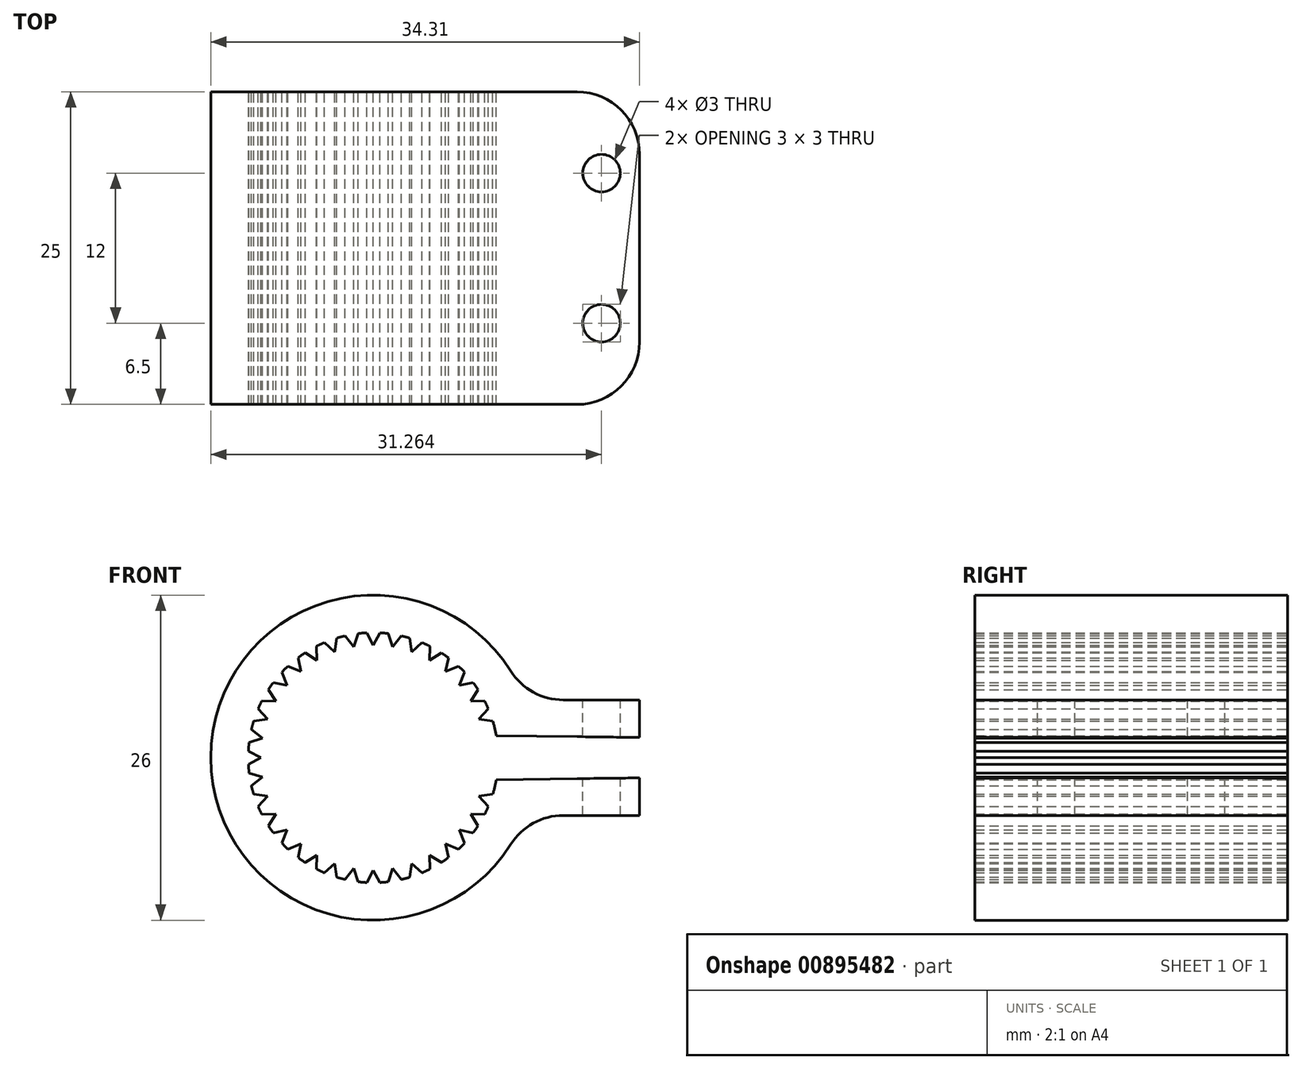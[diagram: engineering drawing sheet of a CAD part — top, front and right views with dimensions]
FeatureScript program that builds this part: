
annotation { "Feature Type Name" : "Feature", "Feature Type Description" : "" }
export const myFeature = defineFeature(function(context is Context, id is Id, definition is map)
    precondition{}
    {
        {
            var Q0;
            Q0=qCreatedBy(makeId("Front.planeOp"),FACE);
            var sketch = newSketch(context, id + "F0", { "sketchPlane" : qUnion([Q0])});
            skArc(sketch, "E0", {"start": v(-3.9, 9.2) * mm, "mid": v(-4.23, 9.06) * mm, "end": v(-4.54, 8.91) * mm});
            skArc(sketch, "E1.0", {"start": v(12.15, 4.62) * mm, "mid": v(-13, 0) * mm, "end": v(12.15, -4.62) * mm});
            skLineSegment(sketch, "E2", {"start": v(-0.52, 9.99) * mm, "end": v(0, 9) * mm});
            skLineSegment(sketch, "E3.MirrorCS", {"start": v(0.52, 9.99) * mm, "end": v(0, 9) * mm});
            skLineSegment(sketch, "E4.1.0", {"start": v(-2.25, 9.74) * mm, "end": v(-1.56, 8.86) * mm});
            skLineSegment(sketch, "E4.1.1", {"start": v(-1.22, 9.93) * mm, "end": v(-1.56, 8.86) * mm});
            skLineSegment(sketch, "E4.2.0", {"start": v(-3.9, 9.2) * mm, "end": v(-3.08, 8.46) * mm});
            skLineSegment(sketch, "E4.2.1", {"start": v(-2.92, 9.56) * mm, "end": v(-3.08, 8.46) * mm});
            skLineSegment(sketch, "E5.2.3.0", {"start": v(-5.45, 8.39) * mm, "end": v(-4.5, 7.8) * mm});
            skLineSegment(sketch, "E5.3.3.0", {"start": v(-4.54, 8.91) * mm, "end": v(-4.5, 7.8) * mm});
            skLineSegment(sketch, "E5.2.4.0", {"start": v(-6.82, 7.31) * mm, "end": v(-5.79, 6.9) * mm});
            skLineSegment(sketch, "E5.3.4.0", {"start": v(-6.02, 7.99) * mm, "end": v(-5.79, 6.9) * mm});
            skLineSegment(sketch, "E5.2.5.0", {"start": v(-7.99, 6.02) * mm, "end": v(-6.9, 5.79) * mm});
            skLineSegment(sketch, "E5.3.5.0", {"start": v(-7.31, 6.82) * mm, "end": v(-6.9, 5.79) * mm});
            skLineSegment(sketch, "E5.2.6.0", {"start": v(-8.91, 4.54) * mm, "end": v(-7.8, 4.5) * mm});
            skLineSegment(sketch, "E5.3.6.0", {"start": v(-8.39, 5.45) * mm, "end": v(-7.8, 4.5) * mm});
            skLineSegment(sketch, "E5.2.7.0", {"start": v(-9.56, 2.92) * mm, "end": v(-8.46, 3.08) * mm});
            skLineSegment(sketch, "E5.3.7.0", {"start": v(-9.2, 3.9) * mm, "end": v(-8.46, 3.08) * mm});
            skLineSegment(sketch, "E5.2.8.0", {"start": v(-9.93, 1.22) * mm, "end": v(-8.86, 1.56) * mm});
            skLineSegment(sketch, "E5.3.8.0", {"start": v(-9.74, 2.25) * mm, "end": v(-8.86, 1.56) * mm});
            skLineSegment(sketch, "E5.2.9.0", {"start": v(-9.99, -0.52) * mm, "end": v(-9, 0) * mm});
            skLineSegment(sketch, "E5.3.9.0", {"start": v(-9.99, 0.52) * mm, "end": v(-9, 0) * mm});
            skLineSegment(sketch, "E6.2.10.0", {"start": v(-9.74, -2.25) * mm, "end": v(-8.86, -1.56) * mm});
            skLineSegment(sketch, "E6.3.10.0", {"start": v(-9.93, -1.22) * mm, "end": v(-8.86, -1.56) * mm});
            skLineSegment(sketch, "E6.2.11.0", {"start": v(-9.2, -3.9) * mm, "end": v(-8.46, -3.08) * mm});
            skLineSegment(sketch, "E6.3.11.0", {"start": v(-9.56, -2.92) * mm, "end": v(-8.46, -3.08) * mm});
            skLineSegment(sketch, "E6.2.12.0", {"start": v(-8.39, -5.45) * mm, "end": v(-7.8, -4.5) * mm});
            skLineSegment(sketch, "E6.3.12.0", {"start": v(-8.91, -4.54) * mm, "end": v(-7.8, -4.5) * mm});
            skLineSegment(sketch, "E6.2.13.0", {"start": v(-7.31, -6.82) * mm, "end": v(-6.9, -5.79) * mm});
            skLineSegment(sketch, "E6.3.13.0", {"start": v(-7.99, -6.02) * mm, "end": v(-6.9, -5.79) * mm});
            skLineSegment(sketch, "E6.2.14.0", {"start": v(-6.02, -7.99) * mm, "end": v(-5.79, -6.9) * mm});
            skLineSegment(sketch, "E6.3.14.0", {"start": v(-6.82, -7.31) * mm, "end": v(-5.79, -6.9) * mm});
            skLineSegment(sketch, "E6.2.15.0", {"start": v(-4.54, -8.91) * mm, "end": v(-4.5, -7.8) * mm});
            skLineSegment(sketch, "E6.3.15.0", {"start": v(-5.45, -8.39) * mm, "end": v(-4.5, -7.8) * mm});
            skLineSegment(sketch, "E6.2.16.0", {"start": v(-2.92, -9.56) * mm, "end": v(-3.08, -8.46) * mm});
            skLineSegment(sketch, "E6.3.16.0", {"start": v(-3.9, -9.2) * mm, "end": v(-3.08, -8.46) * mm});
            skLineSegment(sketch, "E6.2.17.0", {"start": v(-1.22, -9.93) * mm, "end": v(-1.56, -8.86) * mm});
            skLineSegment(sketch, "E6.3.17.0", {"start": v(-2.25, -9.74) * mm, "end": v(-1.56, -8.86) * mm});
            skLineSegment(sketch, "E6.2.18.0", {"start": v(0.52, -9.99) * mm, "end": v(0, -9) * mm});
            skLineSegment(sketch, "E6.3.18.0", {"start": v(-0.52, -9.99) * mm, "end": v(0, -9) * mm});
            skLineSegment(sketch, "E6.2.19.0", {"start": v(2.25, -9.74) * mm, "end": v(1.56, -8.86) * mm});
            skLineSegment(sketch, "E6.3.19.0", {"start": v(1.22, -9.93) * mm, "end": v(1.56, -8.86) * mm});
            skLineSegment(sketch, "E6.2.20.0", {"start": v(3.9, -9.2) * mm, "end": v(3.08, -8.46) * mm});
            skLineSegment(sketch, "E6.3.20.0", {"start": v(2.92, -9.56) * mm, "end": v(3.08, -8.46) * mm});
            skLineSegment(sketch, "E6.2.21.0", {"start": v(5.45, -8.39) * mm, "end": v(4.5, -7.8) * mm});
            skLineSegment(sketch, "E6.3.21.0", {"start": v(4.54, -8.91) * mm, "end": v(4.5, -7.8) * mm});
            skLineSegment(sketch, "E6.2.22.0", {"start": v(6.82, -7.31) * mm, "end": v(5.79, -6.9) * mm});
            skLineSegment(sketch, "E6.3.22.0", {"start": v(6.02, -7.99) * mm, "end": v(5.79, -6.9) * mm});
            skLineSegment(sketch, "E6.2.23.0", {"start": v(7.99, -6.02) * mm, "end": v(6.9, -5.79) * mm});
            skLineSegment(sketch, "E6.3.23.0", {"start": v(7.31, -6.82) * mm, "end": v(6.9, -5.79) * mm});
            skLineSegment(sketch, "E6.2.24.0", {"start": v(8.91, -4.54) * mm, "end": v(7.8, -4.5) * mm});
            skLineSegment(sketch, "E6.3.24.0", {"start": v(8.39, -5.45) * mm, "end": v(7.8, -4.5) * mm});
            skLineSegment(sketch, "E6.2.25.0", {"start": v(9.56, -2.92) * mm, "end": v(8.46, -3.08) * mm});
            skLineSegment(sketch, "E6.3.25.0", {"start": v(9.2, -3.9) * mm, "end": v(8.46, -3.08) * mm});
            skLineSegment(sketch, "E6.2.29.0", {"start": v(9.2, 3.9) * mm, "end": v(8.46, 3.08) * mm});
            skLineSegment(sketch, "E6.3.29.0", {"start": v(9.56, 2.92) * mm, "end": v(8.46, 3.08) * mm});
            skLineSegment(sketch, "E6.2.30.0", {"start": v(8.39, 5.45) * mm, "end": v(7.8, 4.5) * mm});
            skLineSegment(sketch, "E6.3.30.0", {"start": v(8.91, 4.54) * mm, "end": v(7.8, 4.5) * mm});
            skLineSegment(sketch, "E6.2.31.0", {"start": v(7.31, 6.82) * mm, "end": v(6.9, 5.79) * mm});
            skLineSegment(sketch, "E6.3.31.0", {"start": v(7.99, 6.02) * mm, "end": v(6.9, 5.79) * mm});
            skLineSegment(sketch, "E6.2.32.0", {"start": v(6.02, 7.99) * mm, "end": v(5.79, 6.9) * mm});
            skLineSegment(sketch, "E6.3.32.0", {"start": v(6.82, 7.31) * mm, "end": v(5.79, 6.9) * mm});
            skLineSegment(sketch, "E6.2.33.0", {"start": v(4.54, 8.91) * mm, "end": v(4.5, 7.8) * mm});
            skLineSegment(sketch, "E6.3.33.0", {"start": v(5.45, 8.39) * mm, "end": v(4.5, 7.8) * mm});
            skLineSegment(sketch, "E6.2.34.0", {"start": v(2.92, 9.56) * mm, "end": v(3.08, 8.46) * mm});
            skLineSegment(sketch, "E6.3.34.0", {"start": v(3.9, 9.2) * mm, "end": v(3.08, 8.46) * mm});
            skLineSegment(sketch, "E6.2.35.0", {"start": v(1.22, 9.93) * mm, "end": v(1.56, 8.86) * mm});
            skLineSegment(sketch, "E6.3.35.0", {"start": v(2.25, 9.74) * mm, "end": v(1.56, 8.86) * mm});
            skArc(sketch, "E7.trimOffspring", {"start": v(-5.45, 8.39) * mm, "mid": v(-5.74, 8.2) * mm, "end": v(-6.02, 7.99) * mm});
            skArc(sketch, "E8.trimOffspring", {"start": v(-6.82, 7.31) * mm, "mid": v(-7.07, 7.07) * mm, "end": v(-7.31, 6.82) * mm});
            skArc(sketch, "E9.trimOffspring", {"start": v(-7.99, 6.02) * mm, "mid": v(-8.2, 5.74) * mm, "end": v(-8.39, 5.45) * mm});
            skArc(sketch, "E10.trimOffspring", {"start": v(-8.91, 4.54) * mm, "mid": v(-9.06, 4.23) * mm, "end": v(-9.2, 3.9) * mm});
            skArc(sketch, "E11.trimOffspring", {"start": v(-9.56, 2.92) * mm, "mid": v(-9.66, 2.59) * mm, "end": v(-9.74, 2.25) * mm});
            skArc(sketch, "E12.trimOffspring", {"start": v(-9.93, 1.22) * mm, "mid": v(-9.96, 0.87) * mm, "end": v(-9.99, 0.52) * mm});
            skArc(sketch, "E13.trimOffspring", {"start": v(-9.99, -0.52) * mm, "mid": v(-9.96, -0.87) * mm, "end": v(-9.93, -1.22) * mm});
            skArc(sketch, "E14.trimOffspring", {"start": v(-9.74, -2.25) * mm, "mid": v(-9.66, -2.59) * mm, "end": v(-9.56, -2.92) * mm});
            skArc(sketch, "E15.trimOffspring", {"start": v(-9.2, -3.9) * mm, "mid": v(-9.06, -4.23) * mm, "end": v(-8.91, -4.54) * mm});
            skArc(sketch, "E16.trimOffspring", {"start": v(-8.39, -5.45) * mm, "mid": v(-8.2, -5.74) * mm, "end": v(-7.99, -6.02) * mm});
            skArc(sketch, "E17.trimOffspring", {"start": v(-7.31, -6.82) * mm, "mid": v(-7.07, -7.07) * mm, "end": v(-6.82, -7.31) * mm});
            skArc(sketch, "E18.trimOffspring", {"start": v(-6.02, -7.99) * mm, "mid": v(-5.74, -8.2) * mm, "end": v(-5.45, -8.39) * mm});
            skArc(sketch, "E19.trimOffspring", {"start": v(-4.54, -8.91) * mm, "mid": v(-4.23, -9.06) * mm, "end": v(-3.9, -9.2) * mm});
            skArc(sketch, "E20.trimOffspring", {"start": v(-2.92, -9.56) * mm, "mid": v(-2.59, -9.66) * mm, "end": v(-2.25, -9.74) * mm});
            skArc(sketch, "E21.trimOffspring", {"start": v(-1.22, -9.93) * mm, "mid": v(-0.87, -9.96) * mm, "end": v(-0.52, -9.99) * mm});
            skArc(sketch, "E22.trimOffspring", {"start": v(0.52, -9.99) * mm, "mid": v(0.87, -9.96) * mm, "end": v(1.22, -9.93) * mm});
            skArc(sketch, "E23.trimOffspring", {"start": v(2.25, -9.74) * mm, "mid": v(2.59, -9.66) * mm, "end": v(2.92, -9.56) * mm});
            skArc(sketch, "E24.trimOffspring", {"start": v(3.9, -9.2) * mm, "mid": v(4.23, -9.06) * mm, "end": v(4.54, -8.91) * mm});
            skArc(sketch, "E25.trimOffspring", {"start": v(5.45, -8.39) * mm, "mid": v(5.74, -8.2) * mm, "end": v(6.02, -7.99) * mm});
            skArc(sketch, "E26.trimOffspring", {"start": v(6.82, -7.31) * mm, "mid": v(7.07, -7.07) * mm, "end": v(7.31, -6.82) * mm});
            skArc(sketch, "E27.trimOffspring", {"start": v(7.99, -6.02) * mm, "mid": v(8.2, -5.74) * mm, "end": v(8.39, -5.45) * mm});
            skArc(sketch, "E28.trimOffspring", {"start": v(8.91, -4.54) * mm, "mid": v(9.06, -4.23) * mm, "end": v(9.2, -3.9) * mm});
            skArc(sketch, "E29.trimOffspring", {"start": v(9.56, -2.92) * mm, "mid": v(9.72, -2.35) * mm, "end": v(9.84, -1.76) * mm});
            skArc(sketch, "E30.trimOffspring", {"start": v(9.84, 1.76) * mm, "mid": v(9.72, 2.35) * mm, "end": v(9.56, 2.92) * mm});
            skArc(sketch, "E31.trimOffspring", {"start": v(9.2, 3.9) * mm, "mid": v(9.06, 4.23) * mm, "end": v(8.91, 4.54) * mm});
            skArc(sketch, "E32.trimOffspring", {"start": v(8.39, 5.45) * mm, "mid": v(8.2, 5.74) * mm, "end": v(7.99, 6.02) * mm});
            skArc(sketch, "E33.trimOffspring", {"start": v(7.31, 6.82) * mm, "mid": v(7.07, 7.07) * mm, "end": v(6.82, 7.31) * mm});
            skArc(sketch, "E34.trimOffspring", {"start": v(6.02, 7.99) * mm, "mid": v(5.74, 8.2) * mm, "end": v(5.45, 8.39) * mm});
            skArc(sketch, "E35.trimOffspring", {"start": v(4.54, 8.91) * mm, "mid": v(4.23, 9.06) * mm, "end": v(3.9, 9.2) * mm});
            skArc(sketch, "E36.trimOffspring", {"start": v(2.92, 9.56) * mm, "mid": v(2.59, 9.66) * mm, "end": v(2.25, 9.74) * mm});
            skArc(sketch, "E37.trimOffspring", {"start": v(1.22, 9.93) * mm, "mid": v(0.64, 9.98) * mm, "end": v(0.05, 10) * mm});
            skArc(sketch, "E38.trimOffspring", {"start": v(-0.52, 9.99) * mm, "mid": v(-0.87, 9.96) * mm, "end": v(-1.22, 9.93) * mm});
            skArc(sketch, "E39.trimOffspring", {"start": v(-2.25, 9.74) * mm, "mid": v(-2.59, 9.66) * mm, "end": v(-2.92, 9.56) * mm});
            skLineSegment(sketch, "E40", {"start": v(9.84, 1.76) * mm, "end": v(21.31, 1.62) * mm});
            skLineSegment(sketch, "E41.MirrorCS", {"start": v(9.84, -1.76) * mm, "end": v(21.31, -1.62) * mm});
            skLineSegment(sketch, "E42", {"start": v(12.15, 4.62) * mm, "end": v(21.31, 4.62) * mm});
            skLineSegment(sketch, "E43", {"start": v(21.31, 4.62) * mm, "end": v(21.31, 1.62) * mm});
            skLineSegment(sketch, "E44.MirrorCS", {"start": v(12.15, -4.62) * mm, "end": v(21.31, -4.62) * mm});
            skLineSegment(sketch, "E45.MirrorCS", {"start": v(21.31, -4.62) * mm, "end": v(21.31, -1.62) * mm});
            skPoint(sketch, "E46.end.orphan", {"position": v(10.32, 4.62) * mm});
            skPoint(sketch, "E47.MirrorCS.end.orphan", {"position": v(10.32, -4.62) * mm});
            skPoint(sketch, "E47.MirrorCS.start.orphan", {"position": v(9.84, -1.76) * mm});
            skSolve(sketch);
        }
        {
            var Q0;
            Q0=makeQuery(id+"F0.imprint","IMPRINT",FACE,{"disambiguationData":[TD([[makeQuery(id+"F0.imprint","IMPRINT",EDGE,{"derivedFrom":sQuery(id+"F0.wireOp",EDGE,"E0")}),-1.0]])]});
            extrude(context, id + "F1", {"entities" : qUnion([Q0]), "depth" : 25 * mm, "offsetDistance" : 25 * mm});
        }
        {
            var Q0;
            Q0=makeQuery(id+"F1.opExtrude","SWEPT_EDGE",EDGE,{"disambiguationData":[OSD([sQuery(id+"F0.wireOp",EDGE,"E1.0"),sQuery(id+"F0.wireOp",EDGE,"E42")])]});
            var Q1;
            Q1=makeQuery(id+"F1.opExtrude","SWEPT_EDGE",EDGE,{"disambiguationData":[OSD([sQuery(id+"F0.wireOp",EDGE,"E1.0"),sQuery(id+"F0.wireOp",EDGE,"E44.MirrorCS")])]});
            var Q2;
            Q2=makeQuery(id+"F1.opExtrude","CAP_EDGE",EDGE,{"disambiguationData":[OSD([sQuery(id+"F0.wireOp",EDGE,"E43")])],"isStart":false});
            var Q3;
            Q3=makeQuery(id+"F1.opExtrude","CAP_EDGE",EDGE,{"disambiguationData":[OSD([sQuery(id+"F0.wireOp",EDGE,"E45.MirrorCS")])],"isStart":false});
            var Q4;
            Q4=makeQuery(id+"F1.opExtrude","CAP_EDGE",EDGE,{"disambiguationData":[OSD([sQuery(id+"F0.wireOp",EDGE,"E43")])],"isStart":true});
            var Q5;
            Q5=makeQuery(id+"F1.opExtrude","CAP_EDGE",EDGE,{"disambiguationData":[OSD([sQuery(id+"F0.wireOp",EDGE,"E45.MirrorCS")])],"isStart":true});
            fillet(context, id + "F2", {"entities" : qUnion([Q0, Q1, Q2, Q3, Q4, Q5]), "radius" : 5 * mm, "tangentPropagation" : true, "allowEdgeOverflow" : false});
        }
        {
            var Q0;
            Q0=makeQuery(id+"F1.opExtrude","SWEPT_FACE",FACE,{"disambiguationData":[OSD([sQuery(id+"F0.wireOp",EDGE,"E42")])]});
            var sketch = newSketch(context, id + "F3", { "sketchPlane" : qUnion([Q0])});
            skLineSegment(sketch, "E48", {"start": v(21.31, -12.5) * mm, "end": v(15.22, -12.5) * mm, "construction": true});
            skCircle(sketch, "E49", {"center": v(18.26, -6.5) * mm, "radius": 1.5 * mm});
            skPoint(sketch, "E49.centerSnap0", {"position": v(18.26, -12.5) * mm});
            skLineSegment(sketch, "E50", {"start": v(21.31, -5) * mm, "end": v(15.22, -5) * mm, "construction": true});
            skCircle(sketch, "E51.MirrorC", {"center": v(18.26, -18.5) * mm, "radius": 1.5 * mm});
            skSolve(sketch);
        }
        {
            var Q0;
            Q0 = qSketchRegion(id + "F3", true);
            var Q1;
            Q1=makeQuery(id+"F1.opExtrude","SWEPT_FACE",FACE,{"disambiguationData":[OSD([sQuery(id+"F0.wireOp",EDGE,"E44.MirrorCS")])]});
            extrude(context, id + "F4", {"entities" : qUnion([Q0]), "operationType" : NewBodyOperationType.REMOVE, "endBound" : BoundingType.UP_TO_SURFACE, "oppositeDirection" : true, "depth" : 25 * mm, "endBoundEntityFace" : qUnion([Q1]), "offsetDistance" : 25 * mm});
        }
    });
